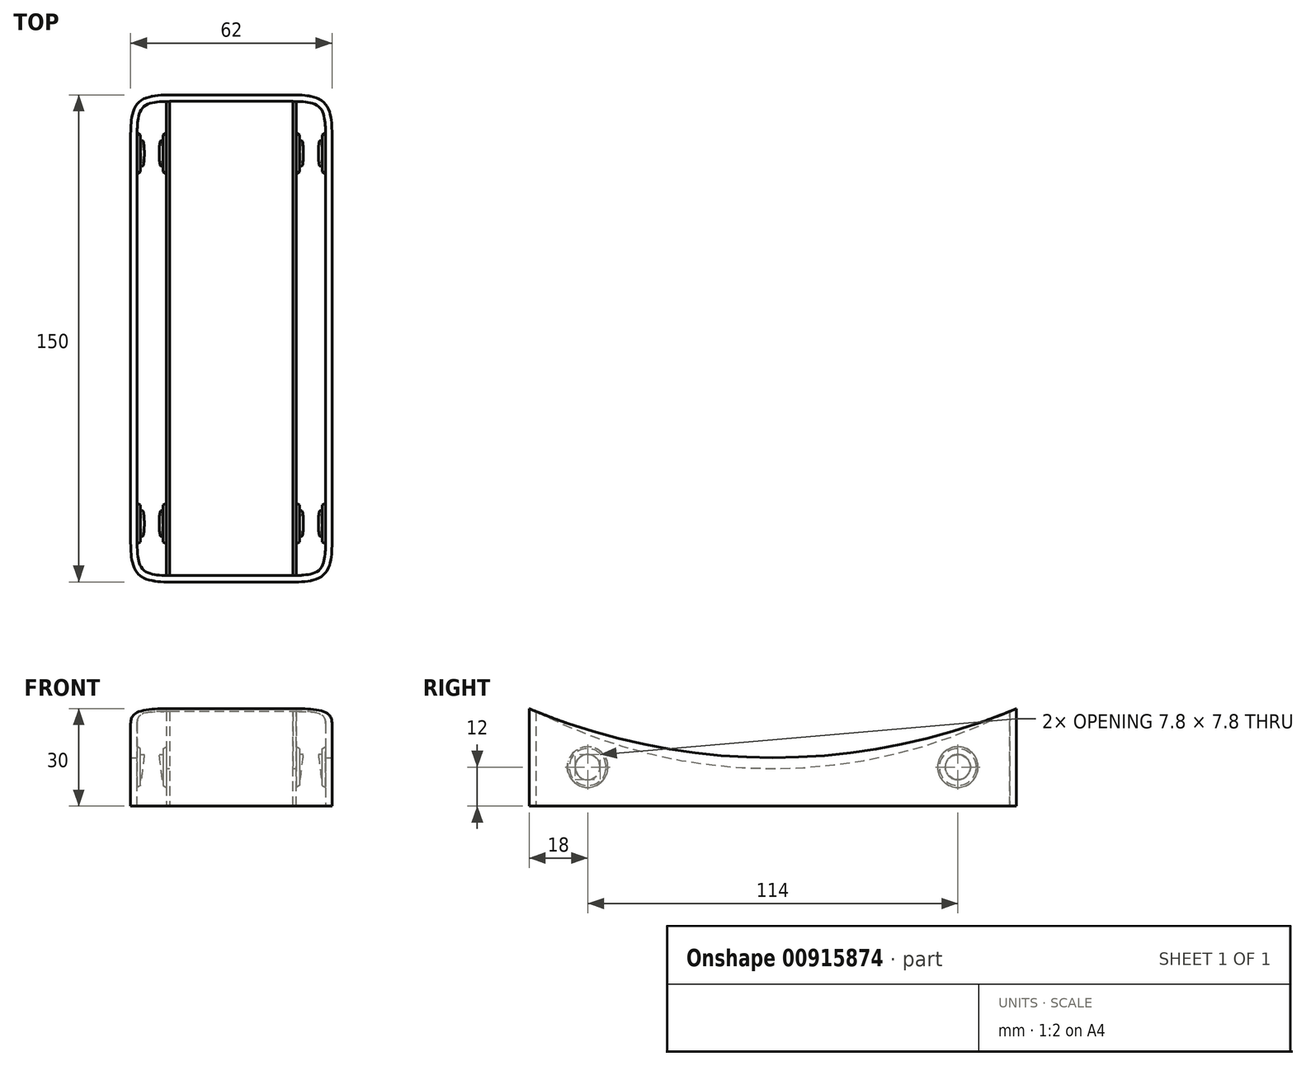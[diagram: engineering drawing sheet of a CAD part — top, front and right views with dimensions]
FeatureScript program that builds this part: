
annotation { "Feature Type Name" : "Feature", "Feature Type Description" : "" }
export const myFeature = defineFeature(function(context is Context, id is Id, definition is map)
    precondition{}
    {
        {
            var Q0;
            Q0=qCreatedBy(makeId("Top.planeOp"),FACE);
            var sketch = newSketch(context, id + "F0", { "sketchPlane" : qUnion([Q0])});
            skLineSegment(sketch, "E0.bottom", {"start": v(-31, 75) * mm, "end": v(31, 75) * mm});
            skLineSegment(sketch, "E0.top", {"start": v(-31, -75) * mm, "end": v(31, -75) * mm});
            skLineSegment(sketch, "E0.left", {"start": v(-31, 75) * mm, "end": v(-31, -75) * mm});
            skLineSegment(sketch, "E0.right", {"start": v(31, 75) * mm, "end": v(31, -75) * mm});
            skPoint(sketch, "E0.middle", {"position": v(0, 0) * mm});
            skSolve(sketch);
        }
        {
            var Q0;
            Q0 = qSketchRegion(id + "F0", true);
            extrude(context, id + "F1", {"entities" : qUnion([Q0]), "depth" : 30 * mm, "offsetDistance" : 25 * mm});
        }
        {
            var Q0;
            Q0=makeQuery(id+"F1.opExtrude","SWEPT_EDGE",EDGE,{"disambiguationData":[OSD([sQuery(id+"F0.wireOp",EDGE,"E0.top"),sQuery(id+"F0.wireOp",EDGE,"E0.right")])]});
            var Q1;
            Q1=makeQuery(id+"F1.opExtrude","SWEPT_EDGE",EDGE,{"disambiguationData":[OSD([sQuery(id+"F0.wireOp",EDGE,"E0.top"),sQuery(id+"F0.wireOp",EDGE,"E0.left")])]});
            var Q2;
            Q2=makeQuery(id+"F1.opExtrude","SWEPT_EDGE",EDGE,{"disambiguationData":[OSD([sQuery(id+"F0.wireOp",EDGE,"E0.bottom"),sQuery(id+"F0.wireOp",EDGE,"E0.right")])]});
            var Q3;
            Q3=makeQuery(id+"F1.opExtrude","SWEPT_EDGE",EDGE,{"disambiguationData":[OSD([sQuery(id+"F0.wireOp",EDGE,"E0.bottom"),sQuery(id+"F0.wireOp",EDGE,"E0.left")])]});
            fillet(context, id + "F2", {"entities" : qUnion([Q0, Q1, Q2, Q3]), "radius" : 12 * mm, "tangentPropagation" : true, "rho" : .6, "crossSection" : FilletCrossSection.CONIC, "allowEdgeOverflow" : false});
        }
        {
            var Q0;
            Q0=makeQuery(id+"F16.boolean.opBoolean","COPY",FACE,{"derivedFrom":makeQuery(id+"F16.opExtrude","SWEPT_FACE",FACE,{"disambiguationData":[OSD([sQuery(id+"F15.wireOp",EDGE,"E15")])]})});
            var Q1;
            Q1=makeQuery(id+"F1.opExtrude","CAP_FACE",FACE,{"disambiguationData":[OSD([sQuery(id+"F0.wireOp",EDGE,"E0.bottom"),sQuery(id+"F0.wireOp",EDGE,"E0.top"),sQuery(id+"F0.wireOp",EDGE,"E0.left"),sQuery(id+"F0.wireOp",EDGE,"E0.right")])],"isStart":true});
            var Q2;
            Q2=makeQuery(id+"F1.opExtrude","CAP_FACE",FACE,{"disambiguationData":[OSD([sQuery(id+"F0.wireOp",EDGE,"E0.bottom"),sQuery(id+"F0.wireOp",EDGE,"E0.top"),sQuery(id+"F0.wireOp",EDGE,"E0.left"),sQuery(id+"F0.wireOp",EDGE,"E0.right")])],"isStart":false});
            shell(context, id + "F3", {"entities" : qUnion([Q0, Q1, Q2]), "thickness" : 2 * mm});
        }
        {
            var Q0;
            Q0=makeQuery(id+"F3.opShell","OFFSET_FACE",FACE,{"disambiguationData":[OSD([sQuery(id+"F0.wireOp",EDGE,"E0.bottom")])]});
            cPlane(context, id + "F4", {"entities" : qUnion([Q0]), "cplaneType" : CPlaneType.OFFSET, "offset" : 16 * mm, "width" : 150 * mm, "height" : 150 * mm});
        }
        {
            var Q0;
            Q0=makeQuery(id+"F3.opShell","OFFSET_FACE",FACE,{"disambiguationData":[OSD([sQuery(id+"F0.wireOp",EDGE,"E0.bottom")])]});
            var sketch = newSketch(context, id + "F5", { "sketchPlane" : qUnion([Q0])});
            skLineSegment(sketch, "E1", {"start": v(-20, 0) * mm, "end": v(-20, 30) * mm});
            skLineSegment(sketch, "E2", {"start": v(-19, 30) * mm, "end": v(-20, 30) * mm});
            skLineSegment(sketch, "E3", {"start": v(-19, 30) * mm, "end": v(-19, 0) * mm});
            skLineSegment(sketch, "E4", {"start": v(-19, 0) * mm, "end": v(-20, 0) * mm});
            skSolve(sketch);
        }
        {
            var Q0;
            Q0=makeQuery(id+"F5.imprint","IMPRINT",FACE,{"disambiguationData":[TD([[makeQuery(id+"F5.imprint","IMPRINT",EDGE,{"derivedFrom":sQuery(id+"F5.wireOp",EDGE,"E1")}),-1.0]])]});
            var Q1;
            Q1=makeQuery(id+"F3.opShell","OFFSET_FACE",FACE,{"disambiguationData":[OSD([sQuery(id+"F0.wireOp",EDGE,"E0.top")])]});
            extrude(context, id + "F6", {"entities" : qUnion([Q0]), "operationType" : NewBodyOperationType.ADD, "endBound" : BoundingType.UP_TO_SURFACE, "depth" : 12 * mm, "endBoundEntityFace" : qUnion([Q1]), "offsetDistance" : 25 * mm});
        }
        {
            var Q0;
            Q0=makeQuery(id+"F6.opExtrude","SWEPT_FACE",FACE,{"disambiguationData":[OSD([sQuery(id+"F5.wireOp",EDGE,"E1")])]});
            var sketch = newSketch(context, id + "F7", { "sketchPlane" : qUnion([Q0])});
            skCircle(sketch, "E5", {"center": v(-57, 12) * mm, "radius": 6.25 * mm});
            skSolve(sketch);
        }
        {
            var Q0;
            Q0 = qSketchRegion(id + "F7", true);
            var Q1;
            Q1=makeQuery(id+"F6.opExtrude","SWEPT_FACE",FACE,{"disambiguationData":[OSD([sQuery(id+"F5.wireOp",EDGE,"E1")])]});
            extrude(context, id + "F8", {"entities" : qUnion([Q0]), "operationType" : NewBodyOperationType.ADD, "depth" : 1 * mm, "endBoundEntityFace" : qUnion([Q1]), "offsetDistance" : 25 * mm, "hasDraft" : true, "draftAngle" : 30 * degree, "draftPullDirection" : true, "hasSecondDirectionDraft" : true, "secondDirectionDraftAngle" : 15 * degree, "secondDirectionDraftPullDirection" : true});
        }
        {
            var Q0;
            Q0=makeQuery(id+"F3.opShell","OFFSET_FACE",FACE,{"disambiguationData":[OSD([sQuery(id+"F0.wireOp",EDGE,"E0.left")])]});
            var sketch = newSketch(context, id + "F9", { "sketchPlane" : qUnion([Q0])});
            skCircle(sketch, "E6.0", {"center": v(57, 12) * mm, "radius": 6.25 * mm});
            skSolve(sketch);
        }
        {
            var Q0;
            Q0 = qSketchRegion(id + "F9", true);
            extrude(context, id + "F10", {"entities" : qUnion([Q0]), "operationType" : NewBodyOperationType.ADD, "depth" : 1 * mm, "offsetDistance" : 25 * mm, "hasDraft" : true, "draftAngle" : 30 * degree, "draftPullDirection" : true});
        }
        {
            var Q0;
            Q0=makeQuery(id+"F8.opExtrude","CAP_FACE",FACE,{"disambiguationData":[OSD([sQuery(id+"F7.wireOp",EDGE,"E5")])],"isStart":false});
            var sketch = newSketch(context, id + "F11", { "sketchPlane" : qUnion([Q0])});
            skCircle(sketch, "E7", {"center": v(-57, 12) * mm, "radius": 3.9 * mm});
            skLineSegment(sketch, "E8", {"start": v(-57, 8.1) * mm, "end": v(-57, 15.9) * mm, "construction": true});
            skSolve(sketch);
        }
        {
            var Q0;
            Q0 = qSketchRegion(id + "F11", true);
            var Q1;
            Q1=makeQuery(id+"F10.opExtrude","CAP_FACE",FACE,{"disambiguationData":[OSD([sQuery(id+"F9.wireOp",EDGE,"E6.0")])],"isStart":false});
            extrude(context, id + "F12", {"entities" : qUnion([Q0]), "operationType" : NewBodyOperationType.ADD, "endBound" : BoundingType.UP_TO_SURFACE, "depth" : 25 * mm, "endBoundEntityFace" : qUnion([Q1]), "offsetDistance" : 25 * mm});
        }
        {
            var Q0;
            Q0=qCreatedBy(id+"F4.planeOp",FACE);
            var sketch = newSketch(context, id + "F13", { "sketchPlane" : qUnion([Q0])});
            skLineSegment(sketch, "E9", {"start": v(-26.8, 15.9) * mm, "end": v(-27.75, 8.1) * mm});
            skLineSegment(sketch, "E10", {"start": v(-27.75, 8.1) * mm, "end": v(-21.25, 8.1) * mm});
            skLineSegment(sketch, "E11", {"start": v(-22.2, 15.9) * mm, "end": v(-21.25, 8.1) * mm});
            skLineSegment(sketch, "E12", {"start": v(-22.2, 15.9) * mm, "end": v(-26.8, 15.9) * mm});
            skLineSegment(sketch, "E13", {"start": v(-21.25, 8.1) * mm, "end": v(-21, 8.1) * mm, "construction": true});
            skLineSegment(sketch, "E14", {"start": v(-27.75, 8.1) * mm, "end": v(-28, 8.1) * mm, "construction": true});
            skSolve(sketch);
        }
        {
            var Q0;
            Q0 = qSketchRegion(id + "F13", true);
            var Q1;
            Q1=makeQuery(id+"F3.opShell","OFFSET_FACE",FACE,{"disambiguationData":[OSD([sQuery(id+"F0.wireOp",EDGE,"E0.bottom"),sQuery(id+"F0.wireOp",EDGE,"E0.left")])]});
            extrude(context, id + "F14", {"entities" : qUnion([Q0]), "operationType" : NewBodyOperationType.REMOVE, "endBound" : BoundingType.SYMMETRIC, "oppositeDirection" : true, "depth" : 12 * mm, "endBoundEntityFace" : qUnion([Q1]), "offsetDistance" : 25 * mm});
        }
        {
            var Q0;
            Q0=makeQuery(id+"F1.opExtrude","SWEPT_FACE",FACE,{"disambiguationData":[OSD([sQuery(id+"F0.wireOp",EDGE,"E0.right")])]});
            var sketch = newSketch(context, id + "F15", { "sketchPlane" : qUnion([Q0])});
            skArc(sketch, "E15", {"start": v(-75, 30) * mm, "mid": v(0, 14.92) * mm, "end": v(75, 30) * mm});
            skLineSegment(sketch, "E16", {"start": v(-75, 30) * mm, "end": v(75, 30) * mm});
            skCircle(sketch, "E17", {"center": v(57, 12) * mm, "radius": 11 * mm, "construction": true});
            skArc(sketch, "E18", {"start": v(0, 2.94) * mm, "mid": v(53.33, 23.3) * mm, "end": v(79.5, 74.05) * mm, "construction": true});
            skLineSegment(sketch, "E19", {"start": v(0, 2.94) * mm, "end": v(-29.27, 2.94) * mm, "construction": true});
            skLineSegment(sketch, "E20", {"start": v(-24.7, 7.25) * mm, "end": v(0, 7.25) * mm, "construction": true});
            skPoint(sketch, "E20.endSnap0", {"position": v(0, 14.92) * mm});
            skArc(sketch, "E21", {"start": v(0, 7.25) * mm, "mid": v(58.45, 26.1) * mm, "end": v(94.85, 75.57) * mm, "construction": true});
            skSolve(sketch);
        }
        {
            var Q0;
            Q0 = qSketchRegion(id + "F15", true);
            extrude(context, id + "F16", {"entities" : qUnion([Q0]), "operationType" : NewBodyOperationType.REMOVE, "endBound" : BoundingType.THROUGH_ALL, "oppositeDirection" : true, "depth" : 25 * mm, "offsetDistance" : 25 * mm});
        }
        {
            var Q0;
            Q0=qCreatedBy(makeId("Front.planeOp"),FACE);
            var sketch = newSketch(context, id + "F17", { "sketchPlane" : qUnion([Q0])});
            skLineSegment(sketch, "E22", {"start": v(0, 0) * mm, "end": v(0, 24.52) * mm, "construction": true});
            skSolve(sketch);
        }
        {
            var Q0;
            Q0=makeQuery(id+"F1.opExtrude","SWEPT_BODY",BODY,{"disambiguationData":[OSD([sQuery(id+"F0.wireOp",EDGE,"E0.bottom"),sQuery(id+"F0.wireOp",EDGE,"E0.top"),sQuery(id+"F0.wireOp",EDGE,"E0.left"),sQuery(id+"F0.wireOp",EDGE,"E0.right")])]});
            var Q1;
            Q1=sQuery(id+"F17.wireOp",EDGE,"E22");
            circularPattern(context, id + "F18", {"operationType" : NewBodyOperationType.ADD, "entities" : qUnion([Q0]), "axis" : qUnion([Q1]), "angle" : 360 * degree, "instanceCount" : 2, "equalSpace" : true});
        }
        {
            var Q0;
            Q0=makeQuery(id+"F1.opExtrude","SWEPT_BODY",BODY,{"disambiguationData":[OSD([sQuery(id+"F0.wireOp",EDGE,"E0.bottom"),sQuery(id+"F0.wireOp",EDGE,"E0.top"),sQuery(id+"F0.wireOp",EDGE,"E0.left"),sQuery(id+"F0.wireOp",EDGE,"E0.right")])]});
            var Q1;
            Q1=qCreatedBy(makeId("Right.planeOp"),FACE);
            mirror(context, id + "F19", {"operationType" : NewBodyOperationType.ADD, "entities" : qUnion([Q0]), "mirrorPlane" : qUnion([Q1])});
        }
        {
            var Q0;
            Q0=qCreatedBy(makeId("Top.planeOp"),FACE);
            var sketch = newSketch(context, id + "F20", { "sketchPlane" : qUnion([Q0])});
            skLineSegment(sketch, "E23.bottom", {"start": v(38.22, 88.74) * mm, "end": v(-49.86, 88.74) * mm});
            skLineSegment(sketch, "E23.top", {"start": v(38.22, 39.81) * mm, "end": v(-49.86, 39.81) * mm});
            skLineSegment(sketch, "E23.left", {"start": v(38.22, 88.74) * mm, "end": v(38.22, 39.81) * mm});
            skLineSegment(sketch, "E23.right", {"start": v(-49.86, 88.74) * mm, "end": v(-49.86, 39.81) * mm});
            skPoint(sketch, "E23.middle", {"position": v(-5.82, 64.28) * mm});
            skSolve(sketch);
        }
        {
            var Q0;
            Q0=makeQuery(id+"F18.opPattern","COPY",FACE,{"derivedFrom":makeQuery(id+"F6.opExtrude","SWEPT_FACE",FACE,{"disambiguationData":[OSD([sQuery(id+"F5.wireOp",EDGE,"E1")])]}),"instanceName":"1"});
            var sketch = newSketch(context, id + "F21", { "sketchPlane" : qUnion([Q0])});
            skLineSegment(sketch, "E24", {"start": v(72.99, 29.17) * mm, "end": v(-72.99, 29.17) * mm});
            skArc(sketch, "E25", {"start": v(-72.99, 29.17) * mm, "mid": v(0, 11.55) * mm, "end": v(72.99, 29.17) * mm});
            skSolve(sketch);
        }
        {
            var Q0;
            Q0 = qSketchRegion(id + "F21", true);
            var Q1;
            Q1=makeQuery(id+"F6.opExtrude","SWEPT_FACE",FACE,{"disambiguationData":[OSD([sQuery(id+"F5.wireOp",EDGE,"E1")])]});
            extrude(context, id + "F22", {"entities" : qUnion([Q0]), "operationType" : NewBodyOperationType.REMOVE, "endBound" : BoundingType.UP_TO_SURFACE, "oppositeDirection" : true, "depth" : 25 * mm, "endBoundEntityFace" : qUnion([Q1]), "offsetDistance" : 25 * mm});
        }
    });
